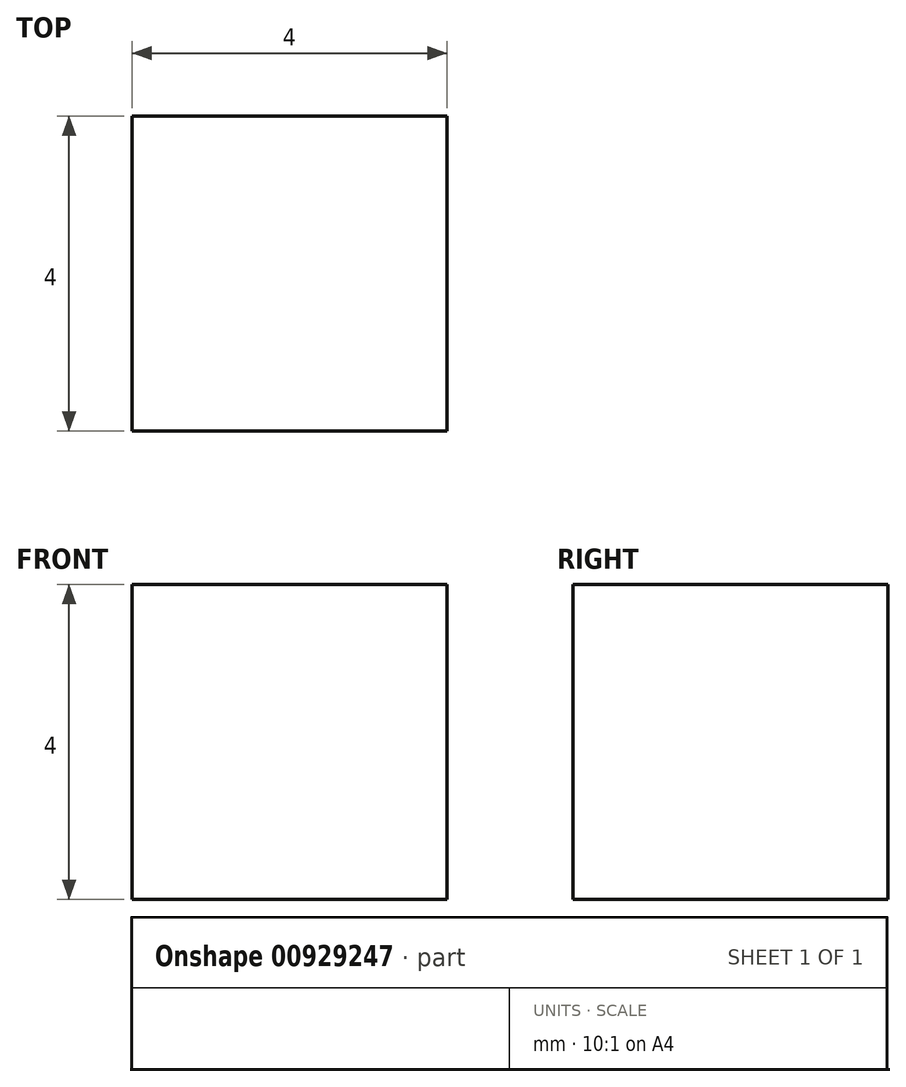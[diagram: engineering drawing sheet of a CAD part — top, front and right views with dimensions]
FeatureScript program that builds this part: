
annotation { "Feature Type Name" : "Feature", "Feature Type Description" : "" }
export const myFeature = defineFeature(function(context is Context, id is Id, definition is map)
    precondition{}
    {
        {
            var Q0;
            Q0=qCreatedBy(makeId("Top.planeOp"),FACE);
            var sketch = newSketch(context, id + "F0", { "sketchPlane" : qUnion([Q0])});
            skLineSegment(sketch, "E0.bottom", {"start": v(0, 0) * mm, "end": v(4, 0) * mm});
            skLineSegment(sketch, "E0.top", {"start": v(0, 4) * mm, "end": v(4, 4) * mm});
            skLineSegment(sketch, "E0.left", {"start": v(0, 0) * mm, "end": v(0, 4) * mm});
            skLineSegment(sketch, "E0.right", {"start": v(4, 0) * mm, "end": v(4, 4) * mm});
            skSolve(sketch);
        }
        {
            var Q0;
            Q0=makeQuery(id+"F0.imprint","IMPRINT",FACE,{"disambiguationData":[TD([[makeQuery(id+"F0.imprint","IMPRINT",EDGE,{"derivedFrom":sQuery(id+"F0.wireOp",EDGE,"E0.bottom")}),1.0]])]});
            extrude(context, id + "F1", {"entities" : qUnion([Q0]), "depth" : 4 * mm, "offsetDistance" : 25 * mm});
        }
    });
